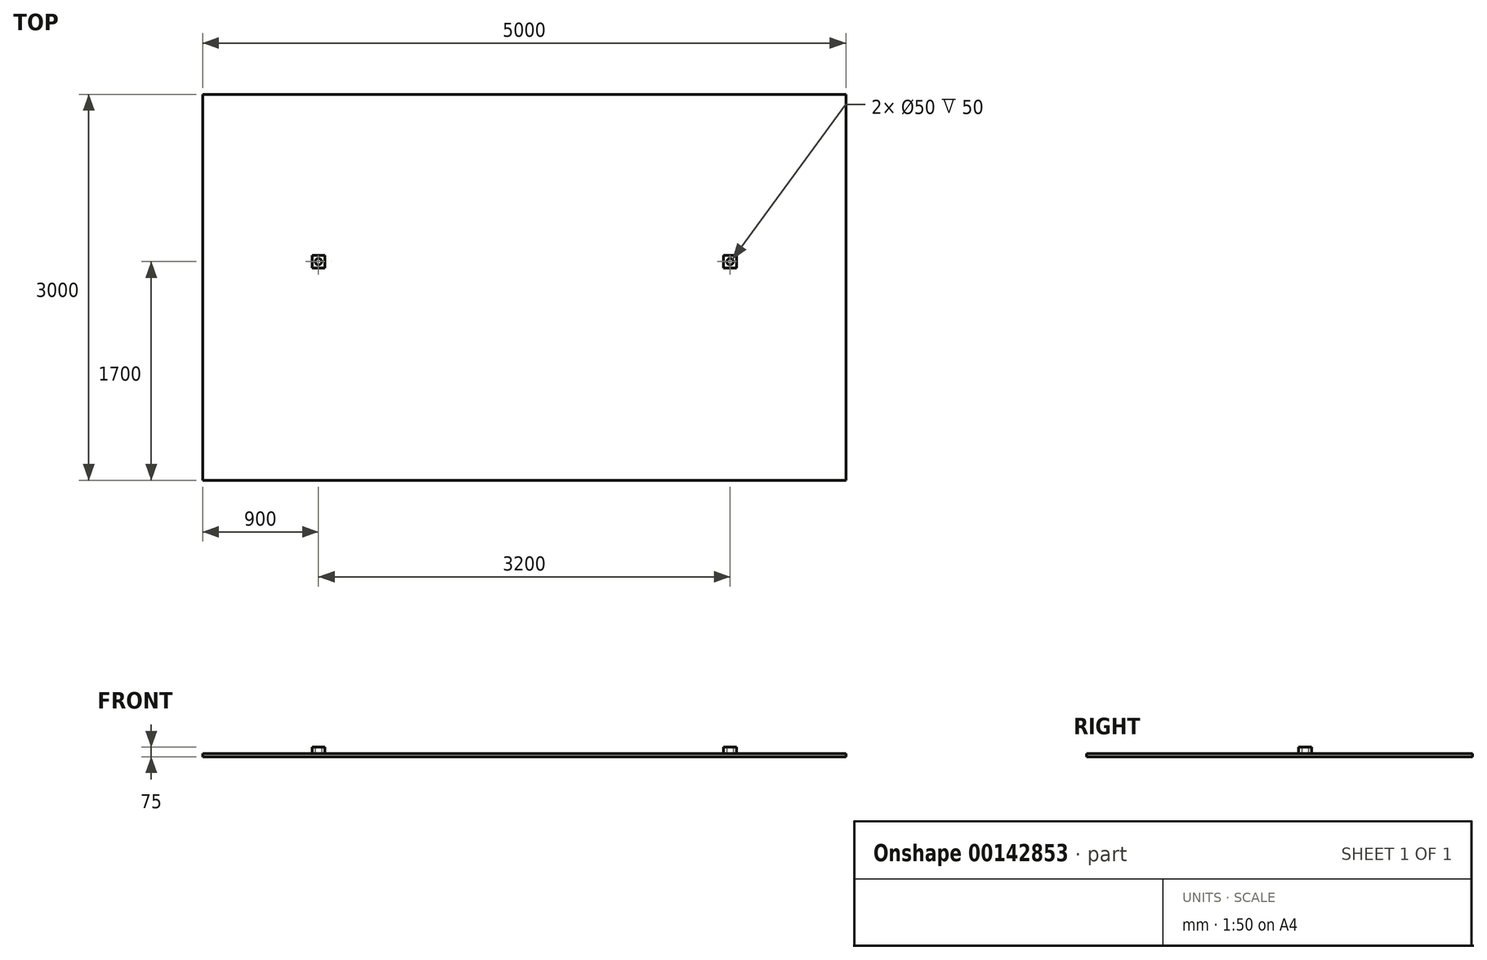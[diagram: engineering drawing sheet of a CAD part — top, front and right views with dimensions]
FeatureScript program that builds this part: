
annotation { "Feature Type Name" : "Feature", "Feature Type Description" : "" }
export const myFeature = defineFeature(function(context is Context, id is Id, definition is map)
    precondition{}
    {
        {
            var Q0;
            Q0=qCreatedBy(makeId("Top.planeOp"),FACE);
            var sketch = newSketch(context, id + "F0", { "sketchPlane" : qUnion([Q0])});
            skLineSegment(sketch, "E0.bottom", {"start": v(0, 0) * mm, "end": v(5000, 0) * mm});
            skLineSegment(sketch, "E0.top", {"start": v(0, 3000) * mm, "end": v(5000, 3000) * mm});
            skLineSegment(sketch, "E0.left", {"start": v(0, 0) * mm, "end": v(0, 3000) * mm});
            skLineSegment(sketch, "E0.right", {"start": v(5000, 0) * mm, "end": v(5000, 3000) * mm});
            skSolve(sketch);
        }
        {
            var Q0;
            Q0 = qSketchRegion(id + "F0", true);
            extrude(context, id + "F1", {"entities" : qUnion([Q0]), "depth" : 25 * mm});
        }
        {
            var Q0;
            Q0=makeQuery(id+"F1.opExtrude","CAP_FACE",FACE,{"disambiguationData":[OSD([sQuery(id+"F0.wireOp",EDGE,"E0.bottom"),sQuery(id+"F0.wireOp",EDGE,"E0.top"),sQuery(id+"F0.wireOp",EDGE,"E0.left"),sQuery(id+"F0.wireOp",EDGE,"E0.right")])],"isStart":false});
            var sketch = newSketch(context, id + "F2", { "sketchPlane" : qUnion([Q0])});
            skLineSegment(sketch, "E1", {"start": v(0, 1500) * mm, "end": v(5000, 1500) * mm});
            skLineSegment(sketch, "E2", {"start": v(2500, 3000) * mm, "end": v(2500, 0) * mm});
            skSolve(sketch);
        }
        {
            var Q0;
            {var subQ0=sQuery(id+"F2.wireOp",EDGE,"E1");var subQ1=makeQuery(id+"F1.opExtrude","CAP_EDGE",EDGE,{"disambiguationData":[OSD([sQuery(id+"F0.wireOp",EDGE,"E0.right")])],"isStart":false});var subQ2=makeQuery(id+"F2.imprint","INTERSECT",VERTEX,{"derivedFrom":[subQ1,subQ0]});Q0=makeQuery(id+"F2.imprint","IMPRINT",FACE,{"disambiguationData":[TD([[makeQuery(id+"F2.imprint","IMPRINT",EDGE,{"disambiguationData":[TD([[subQ2,1.0]])],"derivedFrom":subQ0}),1.0]])]});}
            var sketch = newSketch(context, id + "F3", { "sketchPlane" : qUnion([Q0])});
            skCircle(sketch, "E3", {"center": v(4100, 1700) * mm, "radius": 25 * mm});
            skLineSegment(sketch, "E4.bottom", {"start": v(4050, 1750) * mm, "end": v(4150, 1750) * mm});
            skLineSegment(sketch, "E4.top", {"start": v(4050, 1650) * mm, "end": v(4150, 1650) * mm});
            skLineSegment(sketch, "E4.left", {"start": v(4050, 1750) * mm, "end": v(4050, 1650) * mm});
            skLineSegment(sketch, "E4.right", {"start": v(4150, 1750) * mm, "end": v(4150, 1650) * mm});
            skCircle(sketch, "E5.MirrorC", {"center": v(900, 1700) * mm, "radius": 25 * mm});
            skLineSegment(sketch, "E6.MirrorCS", {"start": v(950, 1650) * mm, "end": v(850, 1650) * mm});
            skLineSegment(sketch, "E7.MirrorCS", {"start": v(850, 1750) * mm, "end": v(850, 1650) * mm});
            skLineSegment(sketch, "E8.MirrorCS", {"start": v(950, 1750) * mm, "end": v(850, 1750) * mm});
            skLineSegment(sketch, "E9.MirrorCS", {"start": v(950, 1750) * mm, "end": v(950, 1650) * mm});
            skSolve(sketch);
        }
        {
            var Q0;
            Q0 = qSketchRegion(id + "F3", true);
            extrude(context, id + "F4", {"entities" : qUnion([Q0]), "operationType" : NewBodyOperationType.ADD, "depth" : 50 * mm});
        }
    });
